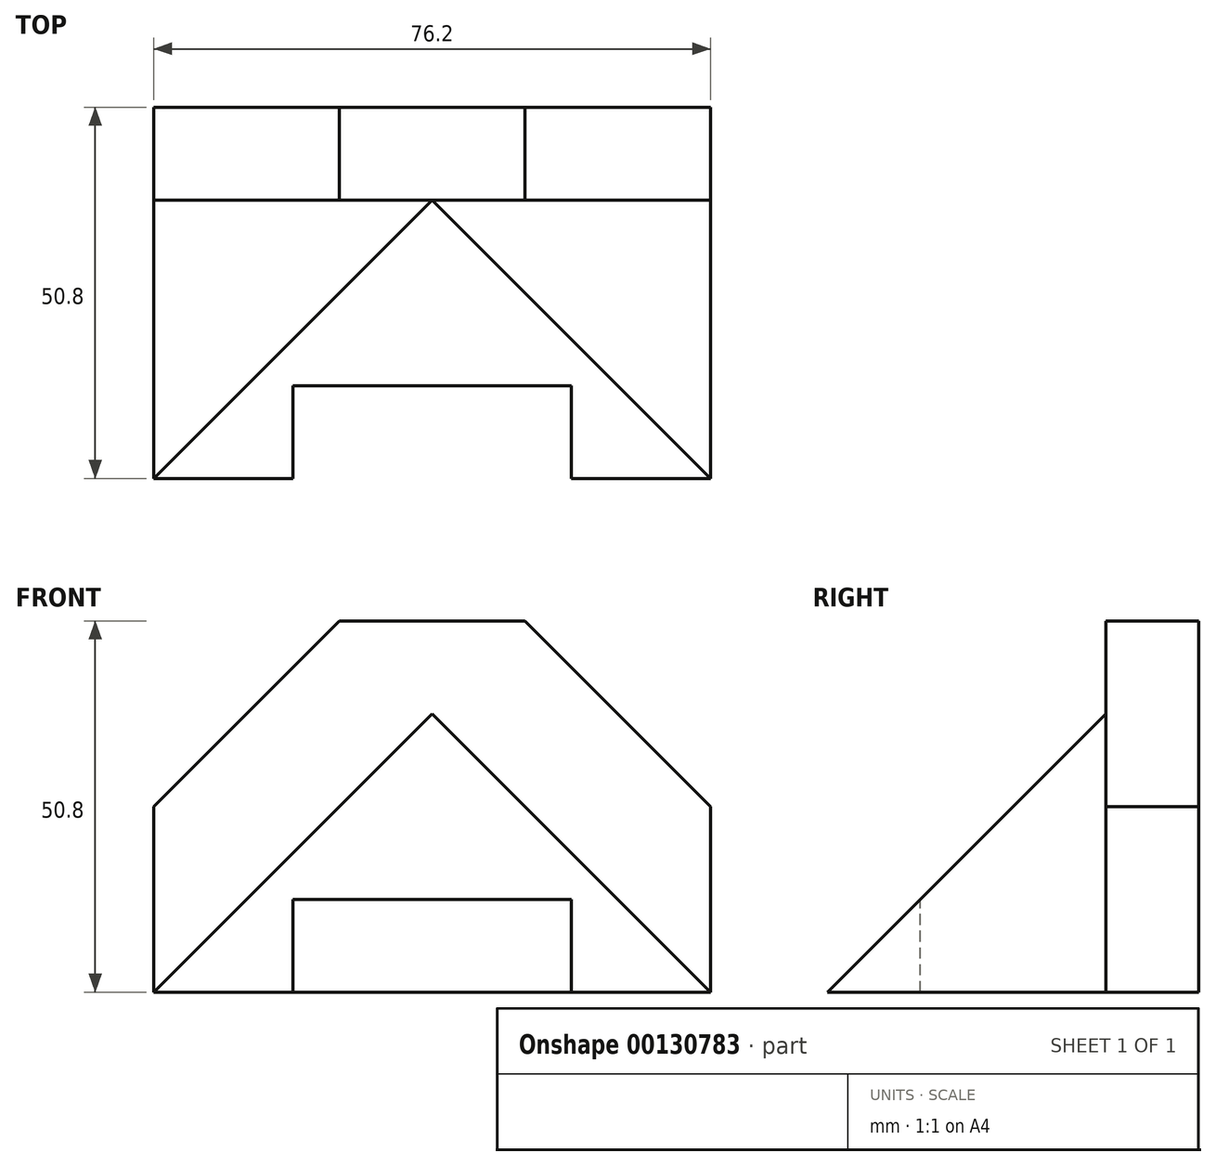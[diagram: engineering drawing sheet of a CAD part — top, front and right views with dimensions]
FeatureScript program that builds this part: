
annotation { "Feature Type Name" : "Feature", "Feature Type Description" : "" }
export const myFeature = defineFeature(function(context is Context, id is Id, definition is map)
    precondition{}
    {
        {
            var Q0;
            Q0=qCreatedBy(makeId("Front.planeOp"),FACE);
            var sketch = newSketch(context, id + "F0", { "sketchPlane" : qUnion([Q0])});
            skLineSegment(sketch, "E0.bottom", {"start": v(0, 0) * mm, "end": v(76.2, 0) * mm});
            skLineSegment(sketch, "E0.top", {"start": v(25.4, 50.8) * mm, "end": v(50.8, 50.8) * mm});
            skLineSegment(sketch, "E0.left", {"start": v(0, 0) * mm, "end": v(0, 25.4) * mm});
            skLineSegment(sketch, "E0.right", {"start": v(76.2, 0) * mm, "end": v(76.2, 50.8) * mm});
            skLineSegment(sketch, "E1", {"start": v(0, 25.4) * mm, "end": v(25.4, 50.8) * mm});
            skLineSegment(sketch, "E2", {"start": v(50.8, 50.8) * mm, "end": v(76.2, 25.4) * mm});
            skPoint(sketch, "E3.orphan", {"position": v(0, 50.8) * mm});
            skSolve(sketch);
        }
        {
            var Q0;
            Q0 = qSketchRegion(id + "F0", true);
            extrude(context, id + "F1", {"entities" : qUnion([Q0]), "depth" : 50.8 * mm});
        }
        {
            var Q0;
            Q0=makeQuery(id+"F1.opExtrude","CAP_FACE",FACE,{"disambiguationData":[OSD([sQuery(id+"F0.wireOp",EDGE,"E0.bottom"),sQuery(id+"F0.wireOp",EDGE,"E0.top"),sQuery(id+"F0.wireOp",EDGE,"E0.left"),sQuery(id+"F0.wireOp",EDGE,"E0.right"),sQuery(id+"F0.wireOp",EDGE,"E1"),sQuery(id+"F0.wireOp",EDGE,"E2")])],"isStart":false});
            var sketch = newSketch(context, id + "F2", { "sketchPlane" : qUnion([Q0])});
            skLineSegment(sketch, "E4", {"start": v(0, 0) * mm, "end": v(38.1, 38.1) * mm});
            skLineSegment(sketch, "E5", {"start": v(38.1, 38.1) * mm, "end": v(76.2, 0) * mm});
            skLineSegment(sketch, "E6", {"start": v(19.05, 0) * mm, "end": v(19.05, 12.7) * mm});
            skLineSegment(sketch, "E7", {"start": v(19.05, 12.7) * mm, "end": v(57.15, 12.7) * mm});
            skLineSegment(sketch, "E8", {"start": v(57.15, 12.7) * mm, "end": v(57.15, 0) * mm});
            skSolve(sketch);
        }
        {
            var Q0;
            Q0=makeQuery(id+"F2.imprint","IMPRINT",FACE,{"disambiguationData":[TD([[makeQuery(id+"F2.imprint","IMPRINT",EDGE,{"derivedFrom":sQuery(id+"F2.wireOp",EDGE,"E4")}),1.0]])]});
            extrude(context, id + "F3", {"entities" : qUnion([Q0]), "operationType" : NewBodyOperationType.REMOVE, "oppositeDirection" : true, "depth" : 38.1 * mm});
        }
        {
            var Q0;
            Q0=makeQuery(id+"F1.opExtrude","SWEPT_FACE",FACE,{"disambiguationData":[OSD([sQuery(id+"F0.wireOp",EDGE,"E0.right")])]});
            var sketch = newSketch(context, id + "F4", { "sketchPlane" : qUnion([Q0])});
            skLineSegment(sketch, "E9", {"start": v(-50.8, 0) * mm, "end": v(-12.7, 38.1) * mm});
            skPoint(sketch, "E9.startSnap0", {"position": v(-6.35, 0) * mm});
            skLineSegment(sketch, "E10", {"start": v(-12.7, 38.1) * mm, "end": v(-12.7, 0) * mm});
            skLineSegment(sketch, "E11", {"start": v(-12.7, 0) * mm, "end": v(-50.8, 0) * mm});
            skLineSegment(sketch, "E12", {"start": v(-50.8, 0) * mm, "end": v(-50.8, 38.1) * mm});
            skLineSegment(sketch, "E13", {"start": v(-50.8, 38.1) * mm, "end": v(-12.7, 38.1) * mm});
            skSolve(sketch);
        }
        {
            var Q0;
            Q0=makeQuery(id+"F4.imprint","IMPRINT",FACE,{"disambiguationData":[TD([[makeQuery(id+"F4.imprint","IMPRINT",EDGE,{"derivedFrom":sQuery(id+"F4.wireOp",EDGE,"E9")}),1.0]])]});
            extrude(context, id + "F5", {"entities" : qUnion([Q0]), "operationType" : NewBodyOperationType.REMOVE, "oppositeDirection" : true, "depth" : 76.2 * mm});
        }
        {
            var Q0;
            {var subQ0=sQuery(id+"F2.wireOp",EDGE,"E6");Q0=makeQuery(id+"F2.imprint","IMPRINT",FACE,{"disambiguationData":[TD([[makeQuery(id+"F2.imprint","IMPRINT",EDGE,{"derivedFrom":subQ0}),-1.0]])]});}
            extrude(context, id + "F6", {"entities" : qUnion([Q0]), "operationType" : NewBodyOperationType.REMOVE, "oppositeDirection" : true, "depth" : 12.7 * mm});
        }
    });
